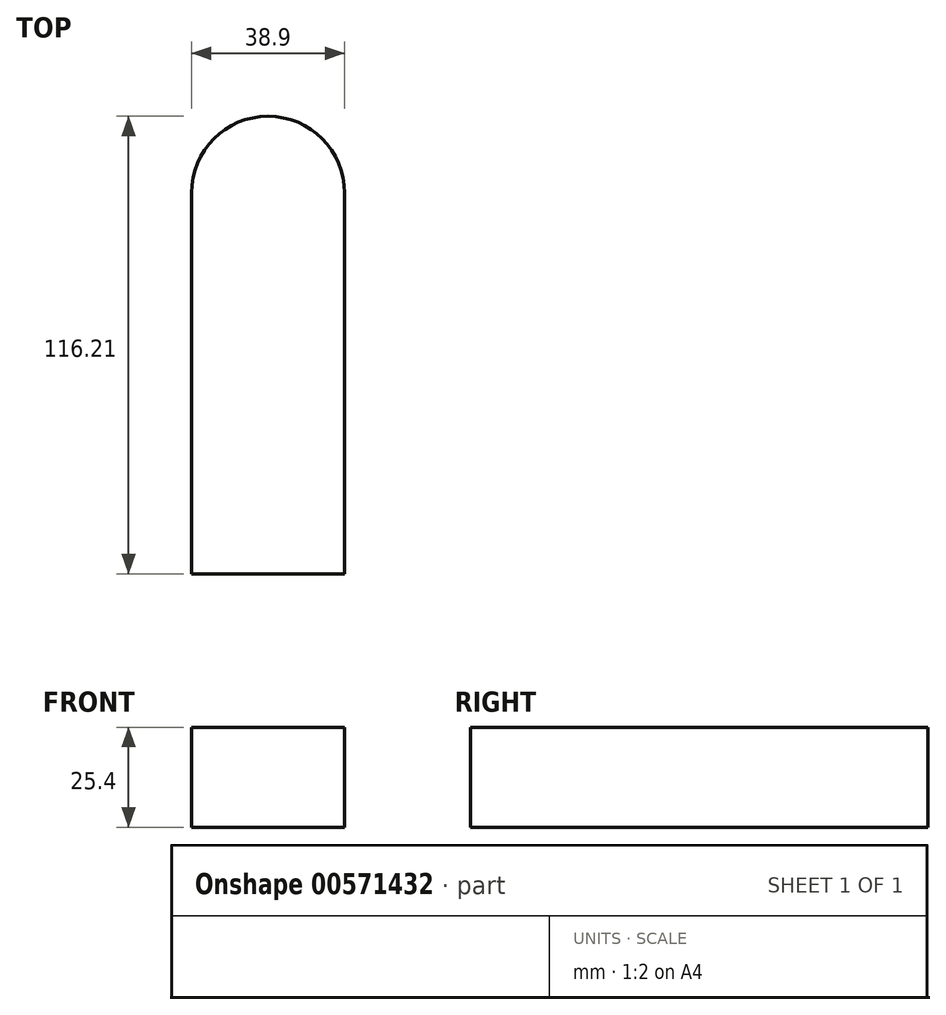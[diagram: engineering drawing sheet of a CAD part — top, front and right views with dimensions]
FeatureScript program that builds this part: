
annotation { "Feature Type Name" : "Feature", "Feature Type Description" : "" }
export const myFeature = defineFeature(function(context is Context, id is Id, definition is map)
    precondition{}
    {
        {
            var Q0;
            Q0=qCreatedBy(makeId("Top.planeOp"),FACE);
            var sketch = newSketch(context, id + "F0", { "sketchPlane" : qUnion([Q0])});
            skLineSegment(sketch, "E0.top", {"start": v(-19.45, -48.38) * mm, "end": v(19.45, -48.38) * mm});
            skLineSegment(sketch, "E0.left", {"start": v(-19.45, 48.38) * mm, "end": v(-19.45, -48.38) * mm});
            skLineSegment(sketch, "E0.right", {"start": v(19.45, 48.38) * mm, "end": v(19.45, -48.38) * mm});
            skPoint(sketch, "E0.middle", {"position": v(0, 0) * mm});
            skArc(sketch, "E1", {"start": v(19.45, 48.38) * mm, "mid": v(0, 67.83) * mm, "end": v(-19.45, 48.38) * mm});
            skSolve(sketch);
        }
        {
            var Q0;
            Q0 = qSketchRegion(id + "F0", true);
            extrude(context, id + "F1", {"entities" : qUnion([Q0]), "depth" : 25.4 * mm, "offsetDistance" : 25.4 * mm});
        }
    });
